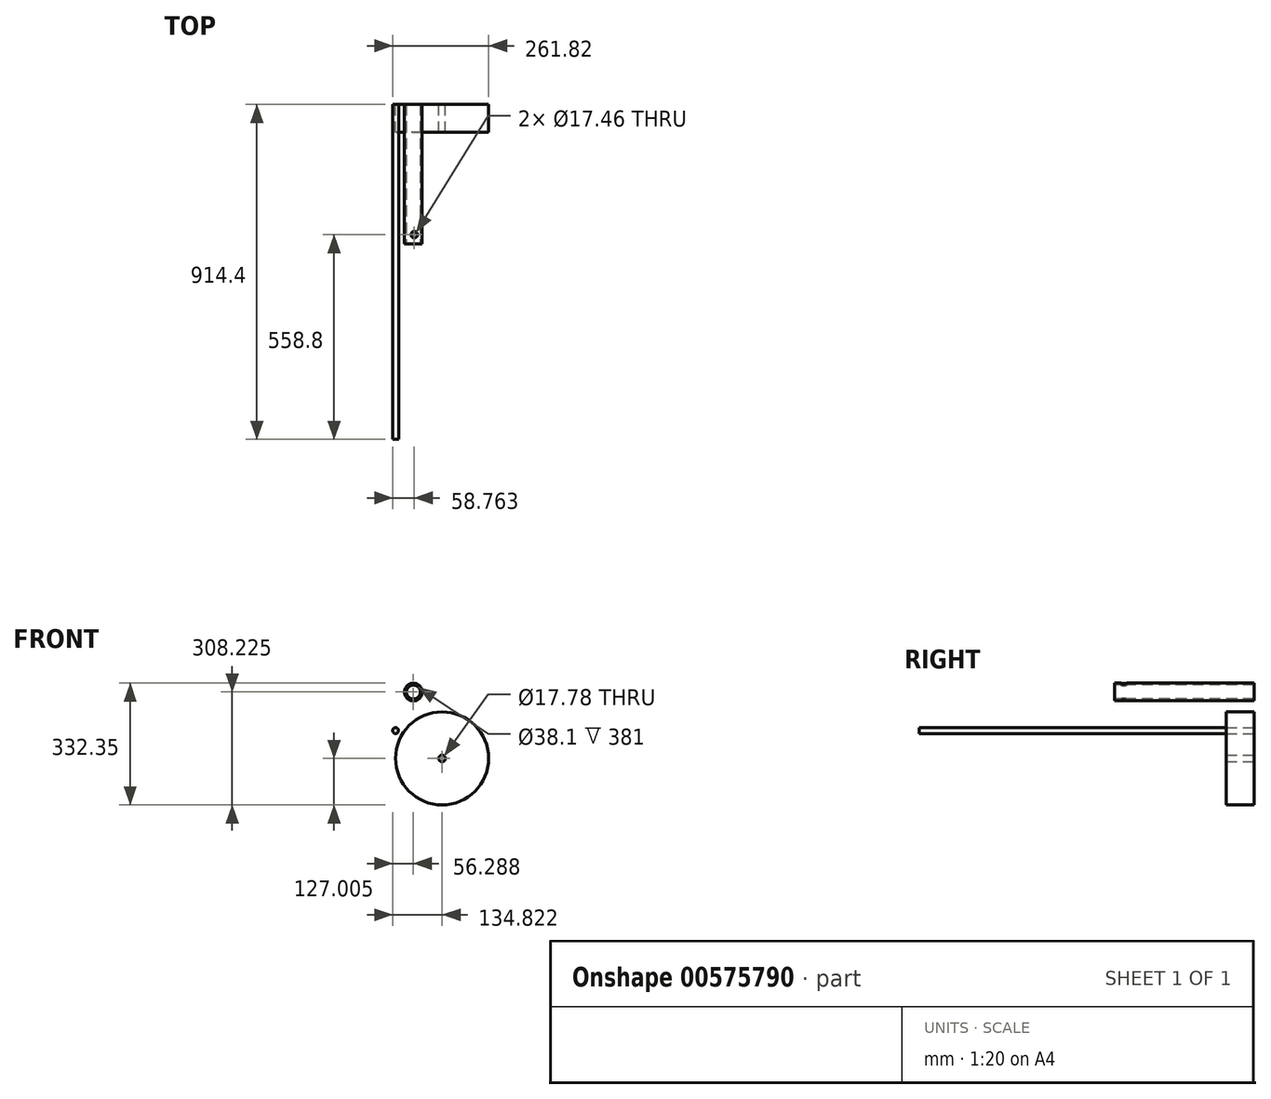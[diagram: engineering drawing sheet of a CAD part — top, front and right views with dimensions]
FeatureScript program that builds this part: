
annotation { "Feature Type Name" : "Feature", "Feature Type Description" : "" }
export const myFeature = defineFeature(function(context is Context, id is Id, definition is map)
    precondition{}
    {
        {
            var Q0;
            Q0=qCreatedBy(makeId("Front.planeOp"),FACE);
            var sketch = newSketch(context, id + "F0", { "sketchPlane" : qUnion([Q0])});
            skCircle(sketch, "E0", {"center": v(-27.2, 32.8) * mm, "radius": 7.94 * mm});
            skCircle(sketch, "E1", {"center": v(99.68, -43) * mm, "radius": 127 * mm});
            skCircle(sketch, "E2", {"center": v(99.68, -43) * mm, "radius": 8.9 * mm});
            skCircle(sketch, "E3", {"center": v(21.15, 138.22) * mm, "radius": 24.13 * mm});
            skSolve(sketch);
        }
        {
            var Q0;
            Q0=makeQuery(id+"F0.imprint","IMPRINT",FACE,{"disambiguationData":[TD([[makeQuery(id+"F0.imprint","IMPRINT",EDGE,{"derivedFrom":sQuery(id+"F0.wireOp",EDGE,"E0")}),1.0]])]});
            extrude(context, id + "F1", {"entities" : qUnion([Q0]), "depth" : 914.4 * mm, "offsetDistance" : 25.4 * mm});
        }
        {
            var Q0;
            Q0=makeQuery(id+"F0.imprint","IMPRINT",FACE,{"disambiguationData":[TD([[makeQuery(id+"F0.imprint","IMPRINT",EDGE,{"derivedFrom":sQuery(id+"F0.wireOp",EDGE,"E1")}),1.0]])]});
            extrude(context, id + "F2", {"entities" : qUnion([Q0]), "depth" : 76.2 * mm, "offsetDistance" : 25.4 * mm});
        }
        {
            var Q0;
            Q0=makeQuery(id+"F0.imprint","IMPRINT",FACE,{"disambiguationData":[TD([[makeQuery(id+"F0.imprint","IMPRINT",EDGE,{"derivedFrom":sQuery(id+"F0.wireOp",EDGE,"E3")}),1.0]])]});
            extrude(context, id + "F3", {"entities" : qUnion([Q0]), "depth" : 381 * mm, "offsetDistance" : 25.4 * mm});
        }
        {
            var Q0;
            Q0=makeQuery(id+"F3.opExtrude","CAP_FACE",FACE,{"disambiguationData":[OSD([sQuery(id+"F0.wireOp",EDGE,"E3")])],"isStart":false});
            var sketch = newSketch(context, id + "F4", { "sketchPlane" : qUnion([Q0])});
            skCircle(sketch, "E4", {"center": v(21.15, 138.22) * mm, "radius": 19.05 * mm});
            skSolve(sketch);
        }
        {
            var Q0;
            Q0=makeQuery(id+"F4.imprint","IMPRINT",FACE,{"disambiguationData":[TD([[makeQuery(id+"F4.imprint","IMPRINT",EDGE,{"derivedFrom":sQuery(id+"F4.wireOp",EDGE,"E4")}),1.0]])]});
            extrude(context, id + "F5", {"entities" : qUnion([Q0]), "operationType" : NewBodyOperationType.REMOVE, "endBound" : BoundingType.THROUGH_ALL, "oppositeDirection" : true, "depth" : 25.4 * mm, "offsetDistance" : 25.4 * mm});
        }
        {
            var Q0;
            Q0=qCreatedBy(makeId("Top.planeOp"),FACE);
            var sketch = newSketch(context, id + "F6", { "sketchPlane" : qUnion([Q0])});
            skLineSegment(sketch, "E5.0", {"start": v(45.28, -381) * mm, "end": v(-2.98, -381) * mm});
            skCircle(sketch, "E6", {"center": v(23.62, -355.6) * mm, "radius": 8.73 * mm});
            skSolve(sketch);
        }
        {
            var Q0;
            Q0 = qSketchRegion(id + "F6", true);
            extrude(context, id + "F7", {"entities" : qUnion([Q0]), "operationType" : NewBodyOperationType.REMOVE, "depth" : 254 * mm, "offsetDistance" : 25.4 * mm});
        }
    });
